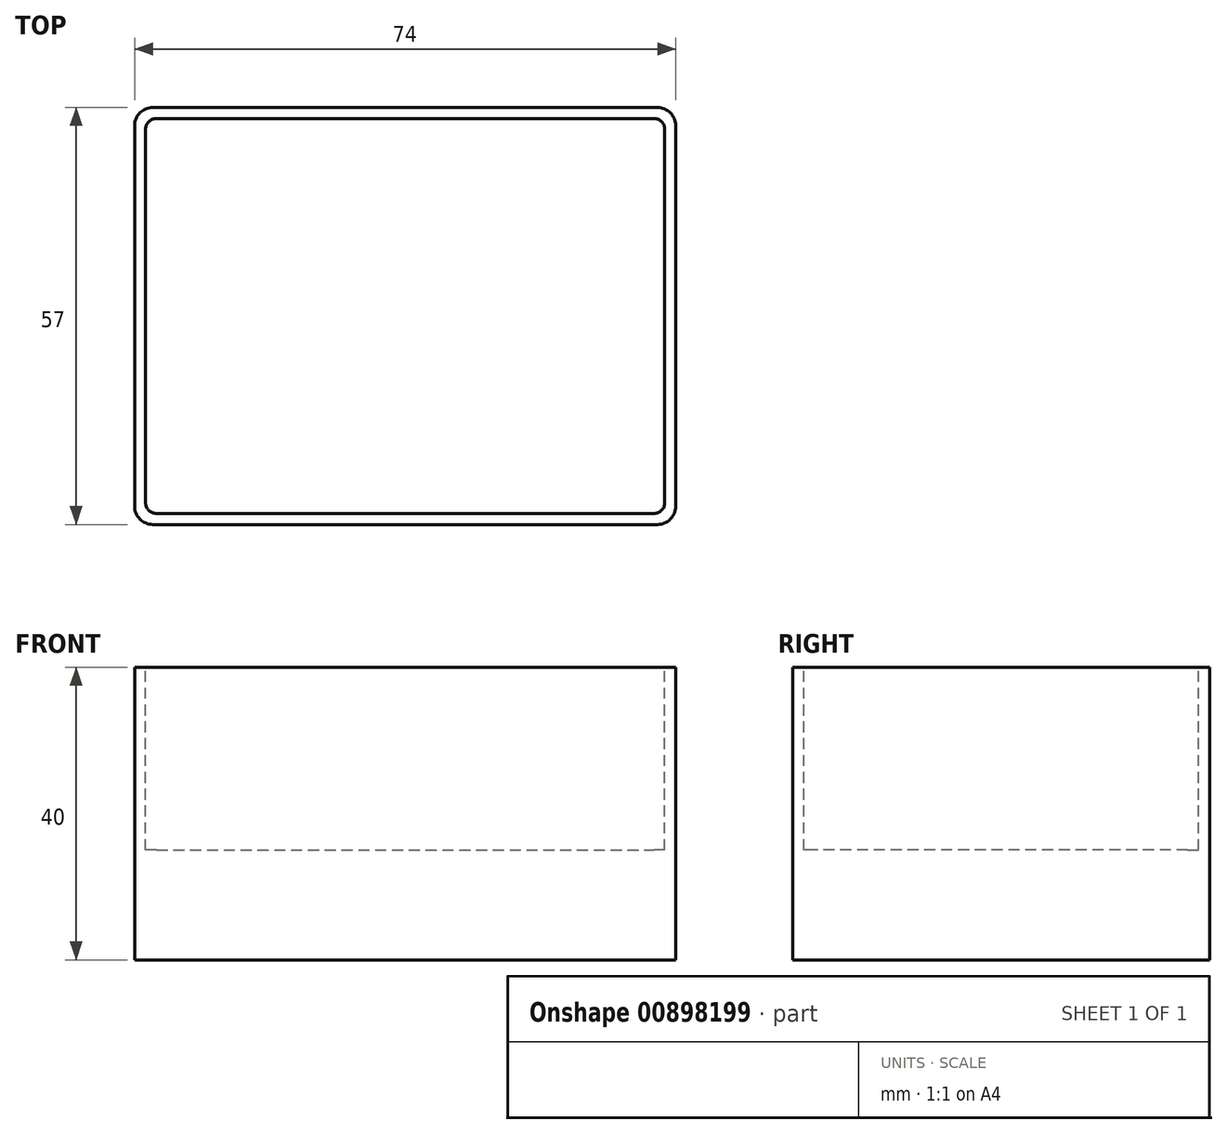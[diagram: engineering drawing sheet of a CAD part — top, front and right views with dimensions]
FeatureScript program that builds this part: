
annotation { "Feature Type Name" : "Feature", "Feature Type Description" : "" }
export const myFeature = defineFeature(function(context is Context, id is Id, definition is map)
    precondition{}
    {
        {
            var Q0;
            Q0=qCreatedBy(makeId("Top.planeOp"),FACE);
            var sketch = newSketch(context, id + "F0", { "sketchPlane" : qUnion([Q0])});
            skLineSegment(sketch, "E0.bottom", {"start": v(-37, 28.5) * mm, "end": v(37, 28.5) * mm});
            skLineSegment(sketch, "E0.top", {"start": v(-37, -28.5) * mm, "end": v(37, -28.5) * mm});
            skLineSegment(sketch, "E0.left", {"start": v(-37, 28.5) * mm, "end": v(-37, -28.5) * mm});
            skLineSegment(sketch, "E0.right", {"start": v(37, 28.5) * mm, "end": v(37, -28.5) * mm});
            skSolve(sketch);
        }
        {
            var Q0;
            Q0 = qSketchRegion(id + "F0", true);
            extrude(context, id + "F1", {"entities" : qUnion([Q0]), "depth" : 40 * mm, "offsetDistance" : 25 * mm});
        }
        {
            var Q0;
            Q0=makeQuery(id+"F1.opExtrude","SWEPT_EDGE",EDGE,{"disambiguationData":[OSD([sQuery(id+"F0.wireOp",EDGE,"E0.bottom"),sQuery(id+"F0.wireOp",EDGE,"E0.right")])]});
            var Q1;
            Q1=makeQuery(id+"F1.opExtrude","SWEPT_EDGE",EDGE,{"disambiguationData":[OSD([sQuery(id+"F0.wireOp",EDGE,"E0.top"),sQuery(id+"F0.wireOp",EDGE,"E0.right")])]});
            var Q2;
            Q2=makeQuery(id+"F1.opExtrude","SWEPT_EDGE",EDGE,{"disambiguationData":[OSD([sQuery(id+"F0.wireOp",EDGE,"E0.top"),sQuery(id+"F0.wireOp",EDGE,"E0.left")])]});
            var Q3;
            Q3=makeQuery(id+"F1.opExtrude","SWEPT_EDGE",EDGE,{"disambiguationData":[OSD([sQuery(id+"F0.wireOp",EDGE,"E0.bottom"),sQuery(id+"F0.wireOp",EDGE,"E0.left")])]});
            fillet(context, id + "F2", {"entities" : qUnion([Q0, Q1, Q2, Q3]), "radius" : 2.5 * mm, "tangentPropagation" : true, "allowEdgeOverflow" : false});
        }
        {
            var Q0;
            Q0=makeQuery(id+"F1.opExtrude","CAP_FACE",FACE,{"disambiguationData":[OSD([sQuery(id+"F0.wireOp",EDGE,"E0.bottom"),sQuery(id+"F0.wireOp",EDGE,"E0.top"),sQuery(id+"F0.wireOp",EDGE,"E0.left"),sQuery(id+"F0.wireOp",EDGE,"E0.right")])],"isStart":false});
            var sketch = newSketch(context, id + "F3", { "sketchPlane" : qUnion([Q0])});
            skLineSegment(sketch, "E1.0", {"start": v(-35.5, 27) * mm, "end": v(35.5, 27) * mm});
            skLineSegment(sketch, "E1.1", {"start": v(-35.5, 27) * mm, "end": v(-35.5, -27) * mm});
            skLineSegment(sketch, "E1.2", {"start": v(-35.5, -27) * mm, "end": v(35.5, -27) * mm});
            skLineSegment(sketch, "E1.3", {"start": v(35.5, 27) * mm, "end": v(35.5, -27) * mm});
            skSolve(sketch);
        }
        {
            var Q0;
            Q0 = qSketchRegion(id + "F3", true);
            extrude(context, id + "F4", {"entities" : qUnion([Q0]), "operationType" : NewBodyOperationType.REMOVE, "oppositeDirection" : true, "depth" : 25 * mm, "offsetDistance" : 25 * mm});
        }
        {
            var Q0;
            Q0=makeQuery(id+"F4.boolean.opBoolean","COPY",EDGE,{"derivedFrom":makeQuery(id+"F4.opExtrude","SWEPT_EDGE",EDGE,{"disambiguationData":[OSD([sQuery(id+"F3.wireOp",EDGE,"E1.2"),sQuery(id+"F3.wireOp",EDGE,"E1.3")])]})});
            var Q1;
            Q1=makeQuery(id+"F4.boolean.opBoolean","COPY",EDGE,{"derivedFrom":makeQuery(id+"F4.opExtrude","SWEPT_EDGE",EDGE,{"disambiguationData":[OSD([sQuery(id+"F3.wireOp",EDGE,"E1.1"),sQuery(id+"F3.wireOp",EDGE,"E1.2")])]})});
            var Q2;
            Q2=makeQuery(id+"F4.boolean.opBoolean","COPY",EDGE,{"derivedFrom":makeQuery(id+"F4.opExtrude","SWEPT_EDGE",EDGE,{"disambiguationData":[OSD([sQuery(id+"F3.wireOp",EDGE,"E1.0"),sQuery(id+"F3.wireOp",EDGE,"E1.1")])]})});
            var Q3;
            Q3=makeQuery(id+"F4.boolean.opBoolean","COPY",EDGE,{"derivedFrom":makeQuery(id+"F4.opExtrude","SWEPT_EDGE",EDGE,{"disambiguationData":[OSD([sQuery(id+"F3.wireOp",EDGE,"E1.0"),sQuery(id+"F3.wireOp",EDGE,"E1.3")])]})});
            fillet(context, id + "F5", {"entities" : qUnion([Q0, Q1, Q2, Q3]), "radius" : 1.5 * mm, "tangentPropagation" : true, "allowEdgeOverflow" : false});
        }
    });
